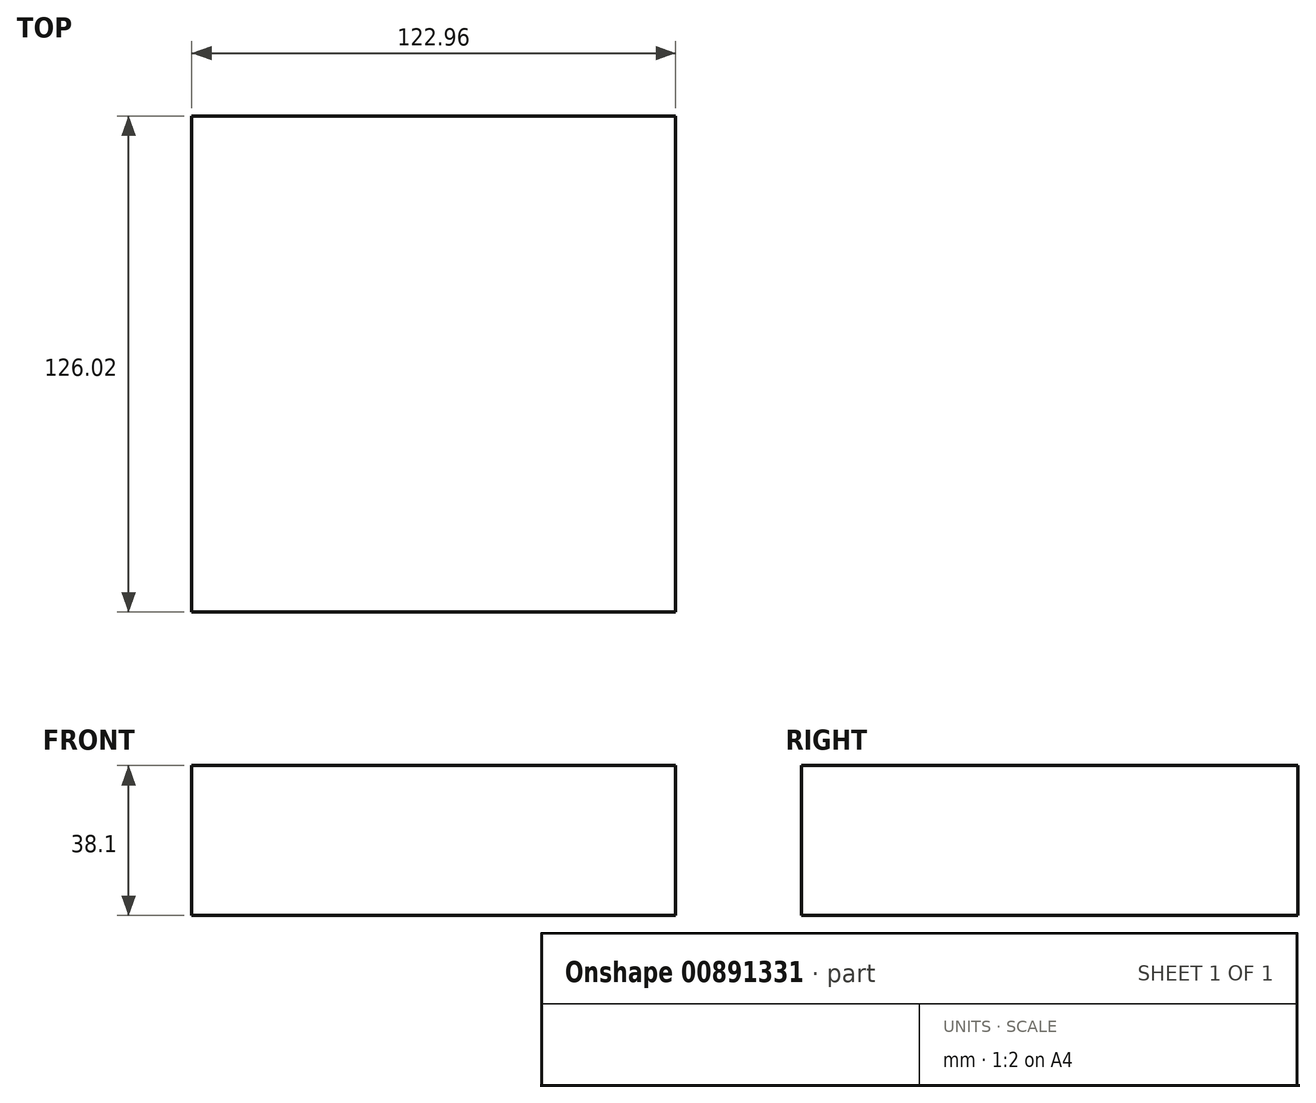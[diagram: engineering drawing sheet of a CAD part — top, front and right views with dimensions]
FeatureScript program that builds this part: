
annotation { "Feature Type Name" : "Feature", "Feature Type Description" : "" }
export const myFeature = defineFeature(function(context is Context, id is Id, definition is map)
    precondition{}
    {
        {
            var Q0;
            Q0=qCreatedBy(makeId("Top.planeOp"),FACE);
            var sketch = newSketch(context, id + "F0", { "sketchPlane" : qUnion([Q0])});
            skLineSegment(sketch, "E0.bottom", {"start": v(-59.45, 35.49) * mm, "end": v(63.51, 35.49) * mm});
            skLineSegment(sketch, "E0.top", {"start": v(-59.45, -39.73) * mm, "end": v(63.51, -39.73) * mm});
            skLineSegment(sketch, "E0.left", {"start": v(-59.45, 35.49) * mm, "end": v(-59.45, -39.73) * mm});
            skLineSegment(sketch, "E0.right", {"start": v(63.51, 35.49) * mm, "end": v(63.51, -39.73) * mm});
            skSolve(sketch);
        }
        {
            var Q0;
            Q0 = qSketchRegion(id + "F0", true);
            extrude(context, id + "F1", {"entities" : qUnion([Q0]), "depth" : 38.1 * mm, "offsetDistance" : 25.4 * mm});
        }
        {
            var Q0;
            Q0=makeQuery(id+"F1.opExtrude","SWEPT_FACE",FACE,{"disambiguationData":[OSD([sQuery(id+"F0.wireOp",EDGE,"E0.bottom")])]});
            extrude(context, id + "F2", {"entities" : qUnion([Q0]), "operationType" : NewBodyOperationType.ADD, "depth" : 25.4 * mm, "offsetDistance" : 25.4 * mm});
        }
        {
            var Q0;
            Q0=makeQuery(id+"F1.opExtrude","SWEPT_FACE",FACE,{"disambiguationData":[OSD([sQuery(id+"F0.wireOp",EDGE,"E0.top")])]});
            extrude(context, id + "F3", {"entities" : qUnion([Q0]), "operationType" : NewBodyOperationType.ADD, "depth" : 25.4 * mm, "offsetDistance" : 25.4 * mm});
        }
    });
